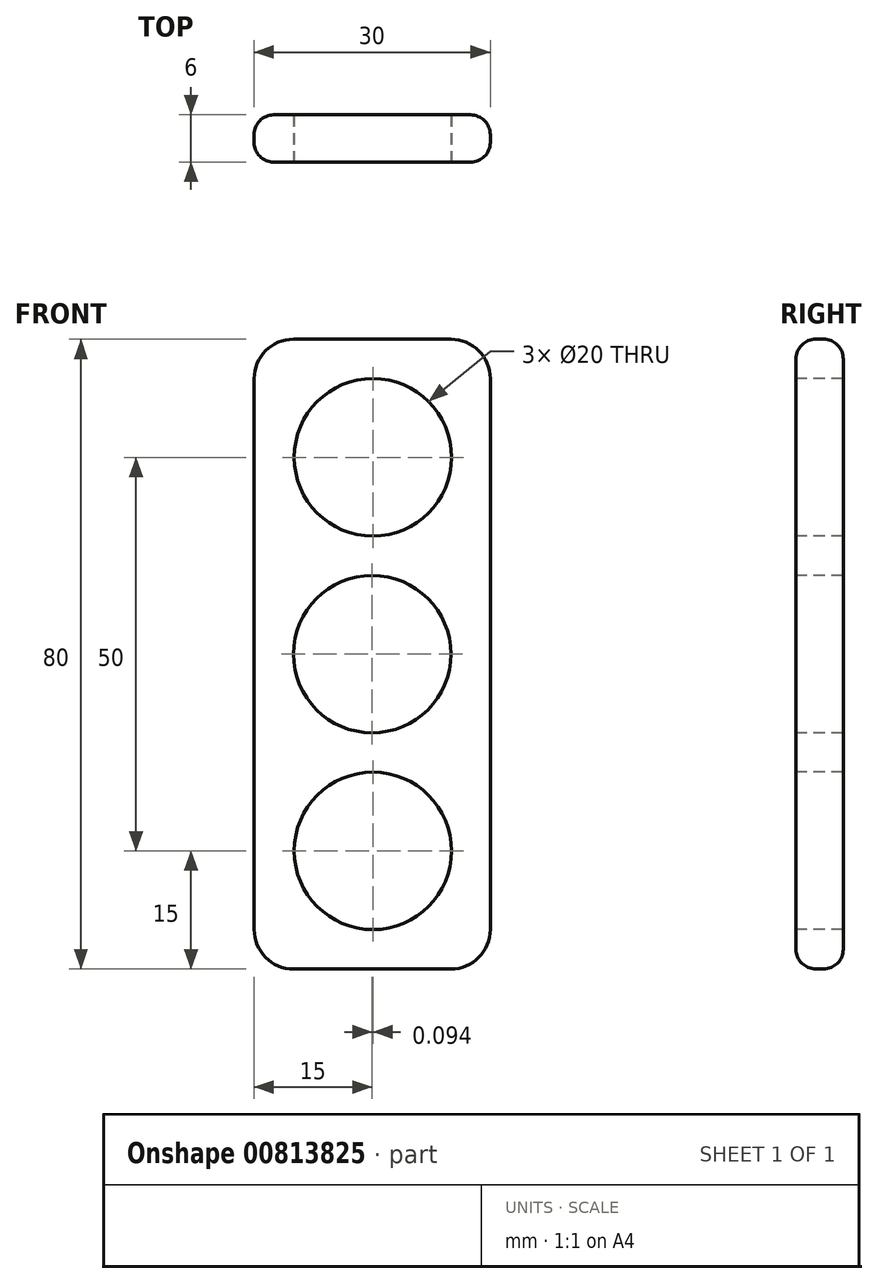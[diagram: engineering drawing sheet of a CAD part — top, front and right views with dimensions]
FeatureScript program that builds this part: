
annotation { "Feature Type Name" : "Feature", "Feature Type Description" : "" }
export const myFeature = defineFeature(function(context is Context, id is Id, definition is map)
    precondition{}
    {
        {
            var Q0;
            Q0=qCreatedBy(makeId("Front.planeOp"),FACE);
            var sketch = newSketch(context, id + "F0", { "sketchPlane" : qUnion([Q0])});
            skLineSegment(sketch, "E0.bottom", {"start": v(0, 0) * mm, "end": v(30, 0) * mm});
            skLineSegment(sketch, "E0.top", {"start": v(0, 80) * mm, "end": v(30, 80) * mm});
            skLineSegment(sketch, "E0.left", {"start": v(0, 0) * mm, "end": v(0, 80) * mm});
            skLineSegment(sketch, "E0.right", {"start": v(30, 0) * mm, "end": v(30, 80) * mm});
            skSolve(sketch);
        }
        {
            var Q0;
            Q0=makeQuery(id+"F0.imprint","IMPRINT",FACE,{"disambiguationData":[TD([[makeQuery(id+"F0.imprint","IMPRINT",EDGE,{"derivedFrom":sQuery(id+"F0.wireOp",EDGE,"E0.bottom")}),1.0]])]});
            extrude(context, id + "F1", {"entities" : qUnion([Q0]), "depth" : 6 * mm, "offsetDistance" : 25 * mm});
        }
        {
            var Q0;
            Q0=makeQuery(id+"F1.opExtrude","SWEPT_EDGE",EDGE,{"disambiguationData":[OSD([sQuery(id+"F0.wireOp",EDGE,"E0.top"),sQuery(id+"F0.wireOp",EDGE,"E0.right")])]});
            fillet(context, id + "F2", {"entities" : qUnion([Q0]), "radius" : 5 * mm, "tangentPropagation" : true, "allowEdgeOverflow" : false});
        }
        {
            var Q0;
            Q0=makeQuery(id+"F1.opExtrude","SWEPT_EDGE",EDGE,{"disambiguationData":[OSD([sQuery(id+"F0.wireOp",EDGE,"E0.top"),sQuery(id+"F0.wireOp",EDGE,"E0.left")])]});
            fillet(context, id + "F3", {"entities" : qUnion([Q0]), "radius" : 5 * mm, "tangentPropagation" : true, "allowEdgeOverflow" : false});
        }
        {
            var Q0;
            Q0=makeQuery(id+"F1.opExtrude","SWEPT_EDGE",EDGE,{"disambiguationData":[OSD([sQuery(id+"F0.wireOp",EDGE,"E0.bottom"),sQuery(id+"F0.wireOp",EDGE,"E0.left")])]});
            fillet(context, id + "F4", {"entities" : qUnion([Q0]), "radius" : 5 * mm, "tangentPropagation" : true, "allowEdgeOverflow" : false});
        }
        {
            var Q0;
            Q0=makeQuery(id+"F1.opExtrude","SWEPT_EDGE",EDGE,{"disambiguationData":[OSD([sQuery(id+"F0.wireOp",EDGE,"E0.bottom"),sQuery(id+"F0.wireOp",EDGE,"E0.right")])]});
            fillet(context, id + "F5", {"entities" : qUnion([Q0]), "radius" : 5 * mm, "tangentPropagation" : true, "allowEdgeOverflow" : false});
        }
        {
            var Q0;
            {var subQ0=sQuery(id+"F0.wireOp",EDGE,"E0.right");var subQ1=sQuery(id+"F0.wireOp",EDGE,"E0.top");Q0=makeQuery(id+"F2.opFillet","BLEND_EDGE",EDGE,{"blendedFrom":[makeQuery(id+"F1.opExtrude","SWEPT_EDGE",EDGE,{"disambiguationData":[OSD([subQ1,subQ0])]}),makeQuery(id+"F1.opExtrude","CAP_FACE",FACE,{"disambiguationData":[OSD([sQuery(id+"F0.wireOp",EDGE,"E0.bottom"),subQ1,sQuery(id+"F0.wireOp",EDGE,"E0.left"),subQ0])],"isStart":false})],"blendedInto":[makeQuery(id+"F1.opExtrude","CAP_FACE",FACE,{"disambiguationData":[OSD([sQuery(id+"F0.wireOp",EDGE,"E0.bottom"),subQ1,sQuery(id+"F0.wireOp",EDGE,"E0.left"),subQ0])],"isStart":false})]});}
            fillet(context, id + "F6", {"entities" : qUnion([Q0]), "radius" : 2.5 * mm, "tangentPropagation" : true, "allowEdgeOverflow" : false});
        }
        {
            var Q0;
            {var subQ0=sQuery(id+"F0.wireOp",EDGE,"E0.right");var subQ1=sQuery(id+"F0.wireOp",EDGE,"E0.top");Q0=makeQuery(id+"F2.opFillet","BLEND_EDGE",EDGE,{"blendedFrom":[makeQuery(id+"F1.opExtrude","SWEPT_EDGE",EDGE,{"disambiguationData":[OSD([subQ1,subQ0])]}),makeQuery(id+"F1.opExtrude","CAP_FACE",FACE,{"disambiguationData":[OSD([sQuery(id+"F0.wireOp",EDGE,"E0.bottom"),subQ1,sQuery(id+"F0.wireOp",EDGE,"E0.left"),subQ0])],"isStart":true})],"blendedInto":[makeQuery(id+"F1.opExtrude","CAP_FACE",FACE,{"disambiguationData":[OSD([sQuery(id+"F0.wireOp",EDGE,"E0.bottom"),subQ1,sQuery(id+"F0.wireOp",EDGE,"E0.left"),subQ0])],"isStart":true})]});}
            fillet(context, id + "F7", {"entities" : qUnion([Q0]), "radius" : 2.5 * mm, "tangentPropagation" : true, "allowEdgeOverflow" : false});
        }
        {
            var Q0;
            Q0=makeQuery(id+"F1.opExtrude","CAP_FACE",FACE,{"disambiguationData":[OSD([sQuery(id+"F0.wireOp",EDGE,"E0.bottom"),sQuery(id+"F0.wireOp",EDGE,"E0.top"),sQuery(id+"F0.wireOp",EDGE,"E0.left"),sQuery(id+"F0.wireOp",EDGE,"E0.right")])],"isStart":false});
            var sketch = newSketch(context, id + "F8", { "sketchPlane" : qUnion([Q0])});
            skCircle(sketch, "E1", {"center": v(15, 40) * mm, "radius": 10 * mm});
            skPoint(sketch, "E2", {"position": v(15, 77.5) * mm});
            skPoint(sketch, "E3", {"position": v(27.5, 40) * mm});
            skSolve(sketch);
        }
        {
            var Q0;
            Q0=sQuery(id+"F8.wireOp",VERTEX,"E1.center");
            var Q1;
            Q1=makeQuery(id+"F1.opExtrude","SWEPT_BODY",BODY,{"disambiguationData":[OSD([sQuery(id+"F0.wireOp",EDGE,"E0.bottom"),sQuery(id+"F0.wireOp",EDGE,"E0.top"),sQuery(id+"F0.wireOp",EDGE,"E0.left"),sQuery(id+"F0.wireOp",EDGE,"E0.right")])]});
            hole(context, id + "F9", {"style" : HoleStyle.SIMPLE, "endStyle" : HoleEndStyle.THROUGH, "holeDiameter" : 20 * mm, "majorDiameter" : 5 * mm, "isTappedThrough" : true, "tappedDepth" : 12 * mm, "tapClearance" : 3, "locations" : qUnion([Q0]), "scope" : qUnion([Q1])});
        }
        {
            var Q0;
            Q0=makeQuery(id+"F8.imprint","IMPRINT",FACE,{"disambiguationData":[TD([[makeQuery(id+"F8.imprint","IMPRINT",EDGE,{"derivedFrom":sQuery(id+"F8.wireOp",EDGE,"E1")}),-1.0]])]});
            var sketch = newSketch(context, id + "F10", { "sketchPlane" : qUnion([Q0])});
            skSolve(sketch);
        }
        {
            var Q0;
            Q0=makeQuery(id+"F10.imprint","IMPRINT",FACE,{"disambiguationData":[TD([[makeQuery(id+"F10.imprint","IMPRINT",EDGE,{"derivedFrom":makeQuery(id+"F8.imprint","IMPRINT",EDGE,{"derivedFrom":sQuery(id+"F8.wireOp",EDGE,"E1")})}),-1.0]])]});
            var sketch = newSketch(context, id + "F11", { "sketchPlane" : qUnion([Q0])});
            skCircle(sketch, "E4", {"center": v(15.1, 65) * mm, "radius": 10 * mm});
            skLineSegment(sketch, "E5", {"start": v(15.1, 78.54) * mm, "end": v(15.1, 4.02) * mm});
            skSolve(sketch);
        }
        {
            var Q0;
            {var subQ9=sQuery(id+"F11.wireOp",EDGE,"E5");var subQ10=sQuery(id+"F11.wireOp",EDGE,"E4");var subQ11=makeQuery(id+"F11.imprint","INTERSECT",VERTEX,{"disambiguationData":[OD(0.0)],"derivedFrom":[subQ10,subQ9]});Q0=makeQuery(id+"F11.imprint","IMPRINT",FACE,{"disambiguationData":[TD([[makeQuery(id+"F11.imprint","IMPRINT",EDGE,{"disambiguationData":[TD([[subQ11,1.0]])],"derivedFrom":subQ10}),-1.0]])]});}
            var sketch = newSketch(context, id + "F12", { "sketchPlane" : qUnion([Q0])});
            skCircle(sketch, "E6", {"center": v(15.1, 15) * mm, "radius": 10 * mm});
            skSolve(sketch);
        }
        {
            var Q0;
            Q0=sQuery(id+"F11.wireOp",VERTEX,"E4.center");
            var Q1;
            Q1=makeQuery(id+"F1.opExtrude","SWEPT_BODY",BODY,{"disambiguationData":[OSD([sQuery(id+"F0.wireOp",EDGE,"E0.bottom"),sQuery(id+"F0.wireOp",EDGE,"E0.top"),sQuery(id+"F0.wireOp",EDGE,"E0.left"),sQuery(id+"F0.wireOp",EDGE,"E0.right")])]});
            hole(context, id + "F13", {"style" : HoleStyle.SIMPLE, "endStyle" : HoleEndStyle.THROUGH, "holeDiameter" : 20 * mm, "majorDiameter" : 5 * mm, "isTappedThrough" : true, "tappedDepth" : 12 * mm, "tapClearance" : 3, "locations" : qUnion([Q0]), "scope" : qUnion([Q1])});
        }
        {
            var Q0;
            Q0=sQuery(id+"F12.wireOp",VERTEX,"E6.center");
            var Q1;
            Q1=makeQuery(id+"F1.opExtrude","SWEPT_BODY",BODY,{"disambiguationData":[OSD([sQuery(id+"F0.wireOp",EDGE,"E0.bottom"),sQuery(id+"F0.wireOp",EDGE,"E0.top"),sQuery(id+"F0.wireOp",EDGE,"E0.left"),sQuery(id+"F0.wireOp",EDGE,"E0.right")])]});
            hole(context, id + "F14", {"style" : HoleStyle.SIMPLE, "endStyle" : HoleEndStyle.THROUGH, "holeDiameter" : 20 * mm, "majorDiameter" : 5 * mm, "isTappedThrough" : true, "tappedDepth" : 12 * mm, "tapClearance" : 3, "locations" : qUnion([Q0]), "scope" : qUnion([Q1])});
        }
    });
